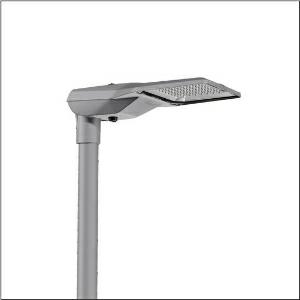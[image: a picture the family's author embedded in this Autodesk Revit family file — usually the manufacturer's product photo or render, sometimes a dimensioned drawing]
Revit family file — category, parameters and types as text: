
# Revit family: streetlight_sl_21_midi___st0_8a_5xe3c63t08lb_8787
name_source: partatom
category: Lighting Fixtures
units: mm (PartAtom-declared; Revit-internal decimal feet)

## family parameters
Cut with Voids When Loaded = No
Host = Face
Light Source = No
Part Type = Normal
Room Calculation Point = No
Round Connector Dimension = Use Diameter
Shared = No

## types (1)
- --- (1 x LED, 12860 lm, 99.6 W, 2700K)
    Apparent Load = 100 VA
    CIE Flux Codes = 38 75 97 100 100
    Color Rendering = 70
    Color Temperature = 2700K
    Default Elevation = 1800 mm
    Description = Streetlight SL 21 midi, mast luminaire, primary light control with lens, of PMMA, primary optical cover: cover, of toughened safety glass, transparent, light distribution: ST0.8a, light emission: direct distribution, primary light characteristic: asymmetric, installation type: side-entry, post-top, LED, High Power LED, rated luminous flux: 12.860lm, luminous efficacy: 129lm/W, light colour: 727, colour temperature: 2700K, control gear: D4i, control: overheat protection, constant luminous flux control, time-dependent luminous flux control, flexible luminous flux parameterisation, pre-setting: logarithmic dimming characteristic, mains connection: 230..240V, AC, 50/60Hz, start of lifetime: 100W, end of service life: 102W, reduction: 45W, luminaire housing, of diecast aluminium, powder-coated, SITECO metallic grey (DB 702S), corrosivity category C5 high according to DIN EN ISO 12944, please order mast flange separately, inclination adjustable: 0°, 5°, 10°, 15°, sealing non-destructively replaceable, multi-level sealing system, length: 644mm, width: 335mm, height: 110mm, mast flange for spigot size: 42mm (side-entry): 5XC10008XM4, 60/48mm (side-entry/post-top): 5XC10108XM2, 76/60mm (side-entry/post-top): 5XC10108XM1, mounting height: 4..8m, Smart Interface below and above, protection rating (complete): IP66, insulation class (complete): insulation class II (safety insulation), certification: CE, ENEC, ENEC+, VDE, impact resistance: IK10, permissible operating ambient temperature for outdoor applications: -40..+50°C, standard-compliant lighting for roads and squares, packaging unit: 1 piece

Light Distribution: ST0.8a
    Height = 111 mm
    Lamp = 1 x LED
    Lamp Light Flux = 12860 lm
    Lamp Power = 99.6 W
    Lamp count = 1
    Length = 644 mm
    Luminous efficacy = 129 lm/W
    Manufacturer = Siteco
    ModVariant = No
    Model = 5XE3C63T08LB
    Number of Poles = 1
    OnlyDefault = Yes
    Power Factor = 1
    Product Name = Streetlight SL 21 midi | ST0.8a
    Product group = mast luminaire | pylon top
    ProductGroupID = 6100
    Protection Class = Protection class II
    Protection Degree = IP 66
    RLX_Detail_Level = 1
    RLX_Emergency_Light_Flux = 0 lm
    RLX_Emergency_Type = 0
    RLX_Emergency_Type_DB = No
    RlxData = <blob elided: 27033 chars, md5=628129d9>
    Socket = socket
    Standby Power = 0 W
    System Light Flux = 12860 lm
    System Power = 100 W
    Type Comments = factory setting: luminous flux: 100 % | dim-lin: 254 | 1020 mA
    Type Image = l_1004304.jpg
    URL = http://relux.com
    VarID = @adj_030931
    Voltage = 0 V
    Weight = 0.00 kg
    Width = 336 mm

## geometry (parser evidence)
native form markers: Blend x4, Sweep x13
no freeform markers — native parametric forms only
